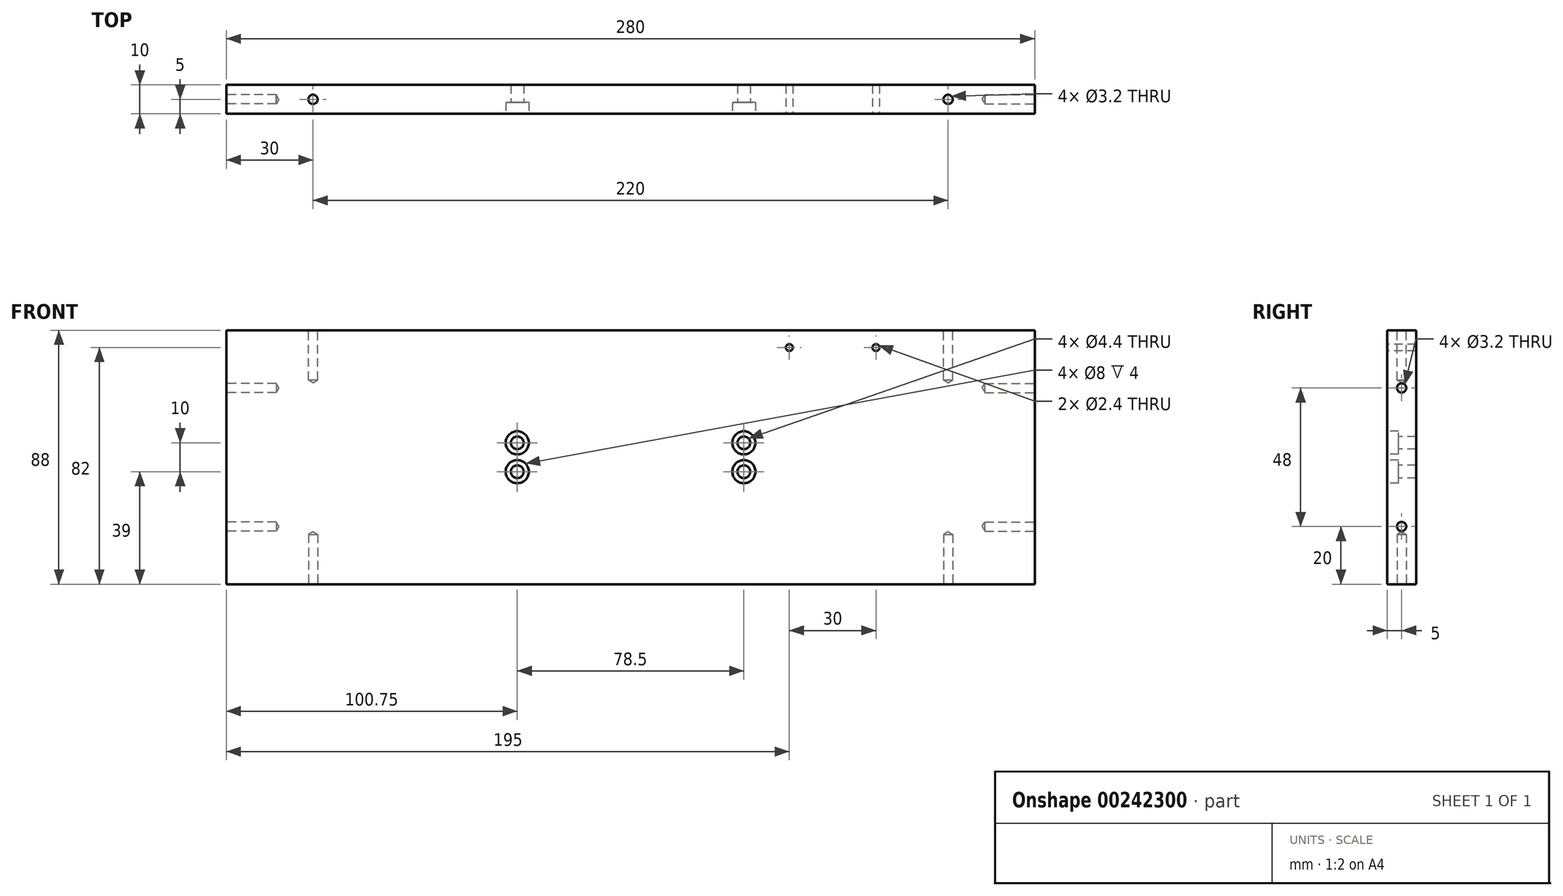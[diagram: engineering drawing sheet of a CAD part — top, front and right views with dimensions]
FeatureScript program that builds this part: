
annotation { "Feature Type Name" : "Feature", "Feature Type Description" : "" }
export const myFeature = defineFeature(function(context is Context, id is Id, definition is map)
    precondition{}
    {
        {
            var Q0;
            Q0=qCreatedBy(makeId("Front.planeOp"),FACE);
            var sketch = newSketch(context, id + "F0", { "sketchPlane" : qUnion([Q0])});
            skLineSegment(sketch, "E0.bottom", {"start": v(140, -44) * mm, "end": v(-140, -44) * mm});
            skLineSegment(sketch, "E0.top", {"start": v(140, 44) * mm, "end": v(-140, 44) * mm});
            skLineSegment(sketch, "E0.left", {"start": v(140, -44) * mm, "end": v(140, 44) * mm});
            skLineSegment(sketch, "E0.right", {"start": v(-140, -44) * mm, "end": v(-140, 44) * mm});
            skPoint(sketch, "E0.middle", {"position": v(0, 0) * mm});
            skSolve(sketch);
        }
        {
            var Q0;
            Q0 = qSketchRegion(id + "F0", true);
            extrude(context, id + "F1", {"entities" : qUnion([Q0]), "endBound" : BoundingType.SYMMETRIC, "depth" : 10 * mm});
        }
        {
            var Q0;
            Q0=makeQuery(id+"F1.opExtrude","SWEPT_FACE",FACE,{"disambiguationData":[OSD([sQuery(id+"F0.wireOp",EDGE,"E0.right")])]});
            var sketch = newSketch(context, id + "F2", { "sketchPlane" : qUnion([Q0])});
            skCircle(sketch, "E1", {"center": v(0, -24) * mm, "radius": 2 * mm});
            skCircle(sketch, "E2.0.1.0", {"center": v(0, 24) * mm, "radius": 2 * mm});
            skLineSegment(sketch, "E2.direction1", {"start": v(0, -24) * mm, "end": v(25, -24) * mm, "construction": true});
            skLineSegment(sketch, "E2.direction2", {"start": v(0, -24) * mm, "end": v(0, 24) * mm, "construction": true});
            skSolve(sketch);
        }
        {
            var Q0;
            Q0=makeQuery(id+"F1.opExtrude","SWEPT_FACE",FACE,{"disambiguationData":[OSD([sQuery(id+"F0.wireOp",EDGE,"E0.left")])]});
            var sketch = newSketch(context, id + "F3", { "sketchPlane" : qUnion([Q0])});
            skCircle(sketch, "E3", {"center": v(0, -24) * mm, "radius": 3.83 * mm});
            skCircle(sketch, "E4.0.1.0", {"center": v(0, 24) * mm, "radius": 3.83 * mm});
            skLineSegment(sketch, "E4.direction1", {"start": v(0, -24) * mm, "end": v(25, -24) * mm, "construction": true});
            skLineSegment(sketch, "E4.direction2", {"start": v(0, -24) * mm, "end": v(0, 24) * mm, "construction": true});
            skSolve(sketch);
        }
        {
            var Q0;
            Q0=makeQuery(id+"F1.opExtrude","SWEPT_FACE",FACE,{"disambiguationData":[OSD([sQuery(id+"F0.wireOp",EDGE,"E0.top")])]});
            var sketch = newSketch(context, id + "F4", { "sketchPlane" : qUnion([Q0])});
            skCircle(sketch, "E5", {"center": v(-110, 0) * mm, "radius": 2 * mm});
            skCircle(sketch, "E6.1.0.0", {"center": v(110, 0) * mm, "radius": 2 * mm});
            skLineSegment(sketch, "E6.direction1", {"start": v(-110, 0) * mm, "end": v(110, 0) * mm, "construction": true});
            skSolve(sketch);
        }
        {
            var Q0;
            Q0=makeQuery(id+"F1.opExtrude","SWEPT_FACE",FACE,{"disambiguationData":[OSD([sQuery(id+"F0.wireOp",EDGE,"E0.bottom")])]});
            var sketch = newSketch(context, id + "F5", { "sketchPlane" : qUnion([Q0])});
            skCircle(sketch, "E7", {"center": v(-110, 0) * mm, "radius": 2 * mm});
            skCircle(sketch, "E8.1.0.0", {"center": v(110, 0) * mm, "radius": 2 * mm});
            skLineSegment(sketch, "E8.direction1", {"start": v(-110, 0) * mm, "end": v(110, 0) * mm, "construction": true});
            skSolve(sketch);
        }
        {
            var Q0;
            Q0=sQuery(id+"F4.wireOp",VERTEX,"E6.direction1.end");
            var Q1;
            Q1=sQuery(id+"F4.wireOp",VERTEX,"E6.direction1.start");
            var Q2;
            Q2=sQuery(id+"F5.wireOp",VERTEX,"E8.direction1.start");
            var Q3;
            Q3=sQuery(id+"F5.wireOp",VERTEX,"E8.1.0.0.center");
            var Q4;
            Q4=sQuery(id+"F3.wireOp",VERTEX,"E4.direction1.start");
            var Q5;
            Q5=sQuery(id+"F3.wireOp",VERTEX,"E4.0.1.0.center");
            var Q6;
            Q6=sQuery(id+"F2.wireOp",VERTEX,"E2.direction1.start");
            var Q7;
            Q7=sQuery(id+"F2.wireOp",VERTEX,"E2.0.1.0.center");
            var Q8;
            Q8=makeQuery(id+"F1.opExtrude","SWEPT_BODY",BODY,{"disambiguationData":[OSD([sQuery(id+"F0.wireOp",EDGE,"E0.bottom"),sQuery(id+"F0.wireOp",EDGE,"E0.top"),sQuery(id+"F0.wireOp",EDGE,"E0.left"),sQuery(id+"F0.wireOp",EDGE,"E0.right")])]});
            hole(context, id + "F6", {"style" : HoleStyle.SIMPLE, "endStyle" : HoleEndStyle.BLIND, "standardTappedOrClearance" : lookupTablePath({ "standard" : "ISO", "engagement" : "75%", "pitch" : "0.75 mm", "size" : "M4", "type" : "Tapped" }), "standardBlindInLast" : lookupTablePath({ "standard" : "ISO", "engagement" : "75%", "pitch" : "0.75 mm", "size" : "M4", "type" : "Tapped" }), "holeDiameter" : 3.2 * mm, "showTappedDepth" : true, "holeDepth" : 17.25 * mm, "tappedDepth" : 15 * mm, "tapClearance" : 3, "locations" : qUnion([Q0, Q1, Q2, Q3, Q4, Q5, Q6, Q7]), "scope" : qUnion([Q8])});
        }
        {
            var Q0;
            Q0=makeQuery(id+"F1.opExtrude","CAP_FACE",FACE,{"disambiguationData":[OSD([sQuery(id+"F0.wireOp",EDGE,"E0.bottom"),sQuery(id+"F0.wireOp",EDGE,"E0.top"),sQuery(id+"F0.wireOp",EDGE,"E0.left"),sQuery(id+"F0.wireOp",EDGE,"E0.right")])],"isStart":false});
            var sketch = newSketch(context, id + "F7", { "sketchPlane" : qUnion([Q0])});
            skCircle(sketch, "E9", {"center": v(39.25, -5) * mm, "radius": 2.15 * mm});
            skCircle(sketch, "E10.0.1.0", {"center": v(39.25, 5) * mm, "radius": 2.15 * mm});
            skCircle(sketch, "E10.1.0.0", {"center": v(-39.25, -5) * mm, "radius": 2.15 * mm});
            skCircle(sketch, "E10.1.1.0", {"center": v(-39.25, 5) * mm, "radius": 2.15 * mm});
            skLineSegment(sketch, "E10.direction1", {"start": v(39.25, -5) * mm, "end": v(-39.25, -5) * mm, "construction": true});
            skLineSegment(sketch, "E10.direction2", {"start": v(39.25, -5) * mm, "end": v(39.25, 5) * mm, "construction": true});
            skSolve(sketch);
        }
        {
            var Q0;
            Q0=sQuery(id+"F7.wireOp",VERTEX,"E10.1.1.0.center");
            var Q1;
            Q1=sQuery(id+"F7.wireOp",VERTEX,"E10.direction2.end");
            var Q2;
            Q2=sQuery(id+"F7.wireOp",VERTEX,"E10.direction1.end");
            var Q3;
            Q3=sQuery(id+"F7.wireOp",VERTEX,"E10.direction2.start");
            var Q4;
            Q4=makeQuery(id+"F1.opExtrude","SWEPT_BODY",BODY,{"disambiguationData":[OSD([sQuery(id+"F0.wireOp",EDGE,"E0.bottom"),sQuery(id+"F0.wireOp",EDGE,"E0.top"),sQuery(id+"F0.wireOp",EDGE,"E0.left"),sQuery(id+"F0.wireOp",EDGE,"E0.right")])]});
            hole(context, id + "F8", {"style" : HoleStyle.C_BORE, "endStyle" : HoleEndStyle.THROUGH, "holeDiameter" : 4.4 * mm, "cBoreDiameter" : 8 * mm, "cBoreDepth" : 4 * mm, "tappedDepth" : 15 * mm, "tapClearance" : 3, "locations" : qUnion([Q0, Q1, Q2, Q3]), "scope" : qUnion([Q4])});
        }
        {
            var Q0;
            Q0=makeQuery(id+"F1.opExtrude","CAP_FACE",FACE,{"disambiguationData":[OSD([sQuery(id+"F0.wireOp",EDGE,"E0.bottom"),sQuery(id+"F0.wireOp",EDGE,"E0.top"),sQuery(id+"F0.wireOp",EDGE,"E0.left"),sQuery(id+"F0.wireOp",EDGE,"E0.right")])],"isStart":false});
            var sketch = newSketch(context, id + "F9", { "sketchPlane" : qUnion([Q0])});
            skCircle(sketch, "E11", {"center": v(85, 38) * mm, "radius": 1.5 * mm});
            skCircle(sketch, "E12.1.0.0", {"center": v(55, 38) * mm, "radius": 1.5 * mm});
            skLineSegment(sketch, "E12.direction1", {"start": v(85, 38) * mm, "end": v(55, 38) * mm, "construction": true});
            skSolve(sketch);
        }
        {
            var Q0;
            Q0=sQuery(id+"F9.wireOp",VERTEX,"E12.direction1.start");
            var Q1;
            Q1=sQuery(id+"F9.wireOp",VERTEX,"E12.1.0.0.center");
            var Q2;
            Q2=makeQuery(id+"F1.opExtrude","SWEPT_BODY",BODY,{"disambiguationData":[OSD([sQuery(id+"F0.wireOp",EDGE,"E0.bottom"),sQuery(id+"F0.wireOp",EDGE,"E0.top"),sQuery(id+"F0.wireOp",EDGE,"E0.left"),sQuery(id+"F0.wireOp",EDGE,"E0.right")])]});
            hole(context, id + "F10", {"style" : HoleStyle.SIMPLE, "endStyle" : HoleEndStyle.THROUGH, "standardTappedOrClearance" : lookupTablePath({ "standard" : "ISO", "engagement" : "75%", "pitch" : "0.6 mm", "size" : "M3", "type" : "Tapped" }), "standardBlindInLast" : lookupTablePath({ "standard" : "ISO", "engagement" : "75%", "pitch" : "0.6 mm", "size" : "M3", "type" : "Tapped" }), "holeDiameter" : 2.4 * mm, "showTappedDepth" : true, "tappedDepth" : 15 * mm, "tapClearance" : 3, "locations" : qUnion([Q0, Q1]), "scope" : qUnion([Q2])});
        }
    });
